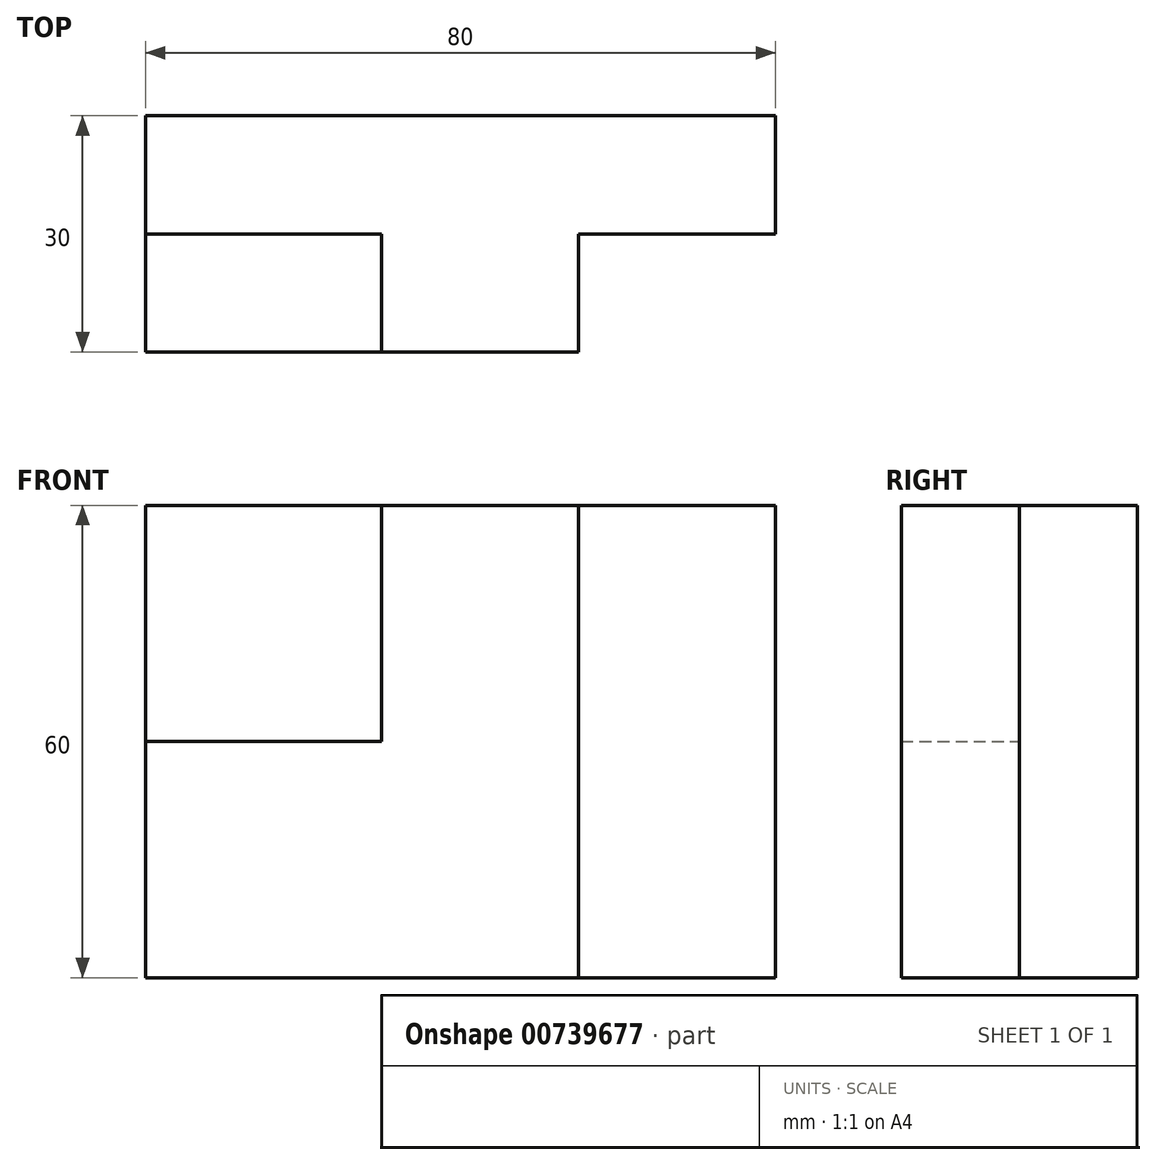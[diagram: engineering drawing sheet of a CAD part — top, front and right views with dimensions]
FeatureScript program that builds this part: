
annotation { "Feature Type Name" : "Feature", "Feature Type Description" : "" }
export const myFeature = defineFeature(function(context is Context, id is Id, definition is map)
    precondition{}
    {
        {
            var Q0;
            Q0=qCreatedBy(makeId("Front.planeOp"),FACE);
            var sketch = newSketch(context, id + "F0", { "sketchPlane" : qUnion([Q0])});
            skLineSegment(sketch, "E0.bottom", {"start": v(0, 0) * mm, "end": v(80, 0) * mm});
            skLineSegment(sketch, "E0.top", {"start": v(0, 60) * mm, "end": v(80, 60) * mm});
            skLineSegment(sketch, "E0.left", {"start": v(0, 0) * mm, "end": v(0, 60) * mm});
            skLineSegment(sketch, "E0.right", {"start": v(80, 0) * mm, "end": v(80, 60) * mm});
            skLineSegment(sketch, "E1", {"start": v(0, 0) * mm, "end": v(0, 30) * mm});
            skLineSegment(sketch, "E2", {"start": v(0, 30) * mm, "end": v(30, 30) * mm});
            skLineSegment(sketch, "E3", {"start": v(30, 30) * mm, "end": v(30, 60) * mm});
            skLineSegment(sketch, "E4", {"start": v(0, 0) * mm, "end": v(55, 0) * mm});
            skLineSegment(sketch, "E5", {"start": v(55, 0) * mm, "end": v(55, 60) * mm});
            skSolve(sketch);
        }
        {
            var Q0;
            {var subQ0=sQuery(id+"F0.wireOp",EDGE,"E2");Q0=makeQuery(id+"F0.imprint","IMPRINT",FACE,{"disambiguationData":[TD([[makeQuery(id+"F0.imprint","IMPRINT",EDGE,{"derivedFrom":subQ0}),-1.0]])]});}
            extrude(context, id + "F1", {"entities" : qUnion([Q0]), "endBound" : BoundingType.SYMMETRIC, "depth" : 30 * mm, "offsetDistance" : 25 * mm});
        }
        {
            var Q0;
            {var subQ4=sQuery(id+"F0.wireOp",EDGE,"E2");Q0=makeQuery(id+"F0.imprint","IMPRINT",FACE,{"disambiguationData":[TD([[makeQuery(id+"F0.imprint","IMPRINT",EDGE,{"derivedFrom":subQ4}),1.0]])]});}
            var Q1;
            {var subQ0=sQuery(id+"F0.wireOp",EDGE,"E0.right");Q1=makeQuery(id+"F0.imprint","IMPRINT",FACE,{"disambiguationData":[TD([[makeQuery(id+"F0.imprint","IMPRINT",EDGE,{"derivedFrom":subQ0}),1.0]])]});}
            extrude(context, id + "F2", {"entities" : qUnion([Q0, Q1]), "operationType" : NewBodyOperationType.ADD, "oppositeDirection" : true, "depth" : 15 * mm, "offsetDistance" : 25 * mm});
        }
    });
